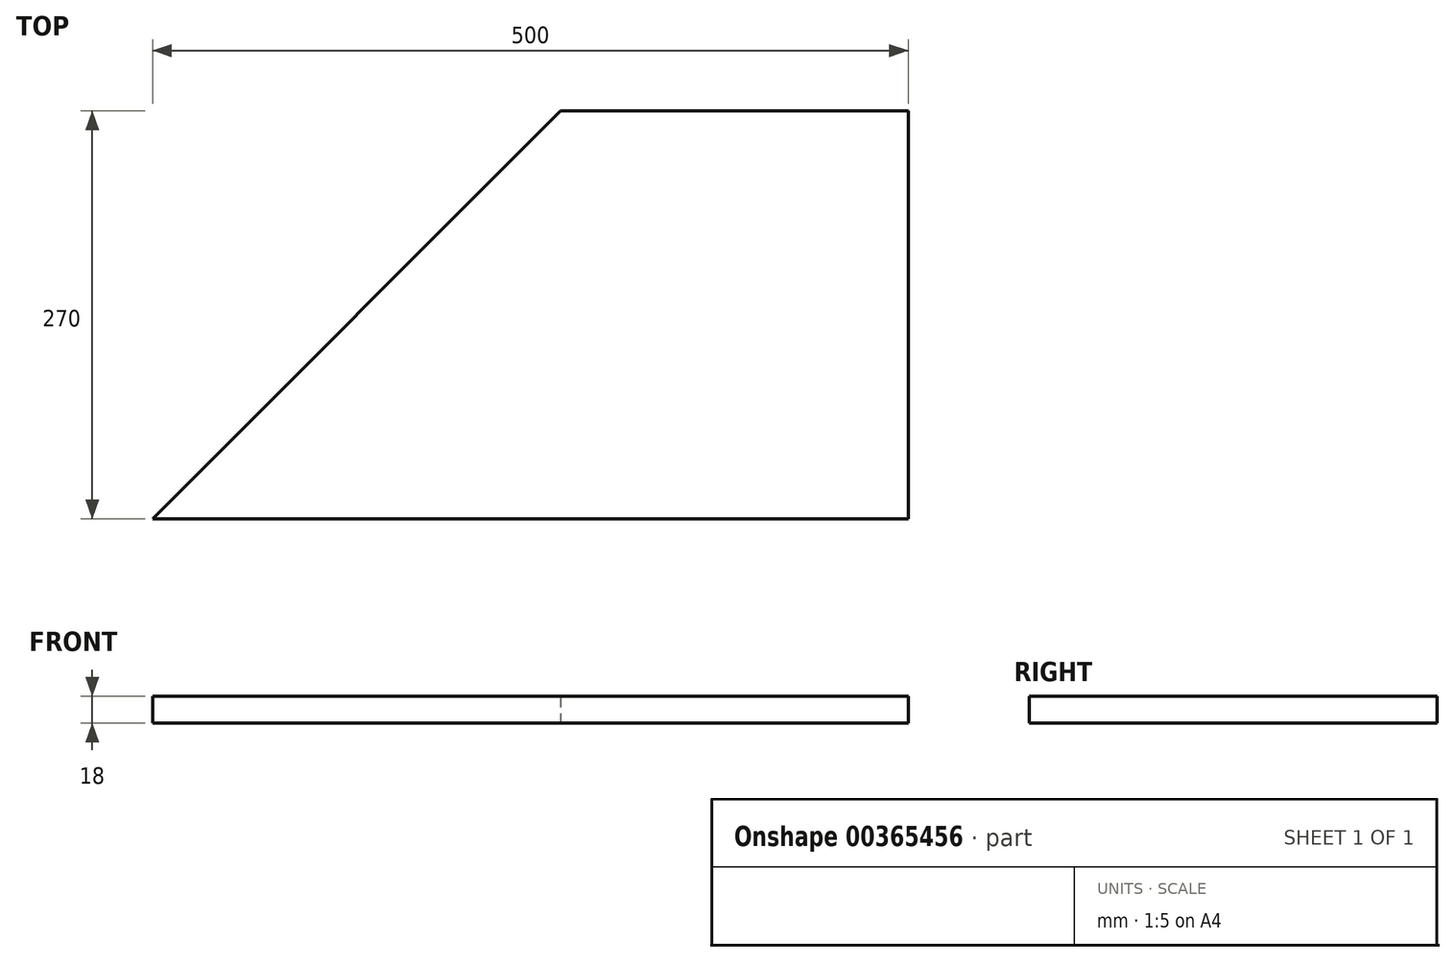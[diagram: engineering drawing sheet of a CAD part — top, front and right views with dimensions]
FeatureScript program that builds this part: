
annotation { "Feature Type Name" : "Feature", "Feature Type Description" : "" }
export const myFeature = defineFeature(function(context is Context, id is Id, definition is map)
    precondition{}
    {
        {
            var Q0;
            Q0=qCreatedBy(makeId("Top.planeOp"),FACE);
            var sketch = newSketch(context, id + "F0", { "sketchPlane" : qUnion([Q0])});
            skLineSegment(sketch, "E0", {"start": v(0, 0) * mm, "end": v(500, 0) * mm});
            skLineSegment(sketch, "E1", {"start": v(270, 270) * mm, "end": v(0, 0) * mm});
            skLineSegment(sketch, "E2", {"start": v(500, 270) * mm, "end": v(270, 270) * mm});
            skLineSegment(sketch, "E3", {"start": v(500, 0) * mm, "end": v(500, 270) * mm});
            skSolve(sketch);
        }
        {
            var Q0;
            Q0=makeQuery(id+"F0.imprint","IMPRINT",FACE,{"disambiguationData":[TD([[makeQuery(id+"F0.imprint","IMPRINT",EDGE,{"derivedFrom":sQuery(id+"F0.wireOp",EDGE,"E0")}),1.0]])]});
            extrude(context, id + "F1", {"entities" : qUnion([Q0]), "depth" : 18 * mm});
        }
    });
